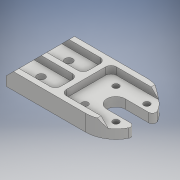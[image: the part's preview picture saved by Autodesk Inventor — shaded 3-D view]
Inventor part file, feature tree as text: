
AUTODESK INVENTOR PART (.ipt)
format: ipt  version: 2018 (Build 220112000, 112)  size: 236,544 bytes
history: native  units: mm
features: extrude x6, sketch x6, fillet x2, projected_geometry x2, chamfer x1
ambient origin geometry x8: Origin, YZ Plane, XZ Plane, XY Plane, X Axis, Y Axis, Z Axis, Center Point
bodies: Solid1 (feature_tree)
feature tree (17):
  extrude  "Extrusion1"  Depth=33.5mm
  extrude  "Extrusion2"  Depth=43.5mm
  extrude  "Extrusion3"  TaperAngle=45.0deg  [1 undecoded]
  extrude  "Extrusion4"  Depth=3.3mm
  extrude  "Extrusion5"  Depth=6.0mm TaperAngle=0.0deg
  fillet  "Fillet1"  Radius=4.2mm
  chamfer  "Chamfer1"  Distance=6.0mm
  extrude  "Extrusion6"  Depth=3.0mm
  fillet  "Fillet2"  Radius=3.0mm
  sketch  "Sketch1"  dims[d0=10.0mm d1=33.5mm]
  sketch  "Sketch2"  dims[d2=16.0mm d3=43.5mm]
  sketch  "Sketch3"  dims[d4=5.0mm d5=0.0mm d6=45.0deg]
  sketch  "Sketch4"  dims[d7=12.0mm d8=3.3mm]
  sketch  "Sketch5"  dims[d9=40.0mm d11=360.0deg d13=6.0mm d14=0.0mm d15=4.2mm]
  projected_geometry  "Projected Loop1"
  sketch  "Sketch6"  dims[d16=10.0mm d18=6.0mm d19=0.0mm d20=3.0mm d21=3.0mm d23=24.0mm d24=1.5mm d25=4.0mm d26=0.0mm d27=4.0mm d28=0.0mm d29=2.0mm d30=4.0mm d31=2.0mm d32=45.0deg d33=45.0deg d34=4.0mm d35=0.0mm d36=3.0mm d37=9.125mm]
  projected_geometry  "Projected Loop2"
note: 1 required parameter value undecoded (feature->parameter linkage not recoverable at this tier; creation-order binding heuristic only, values carry confidence <= 0.55)
